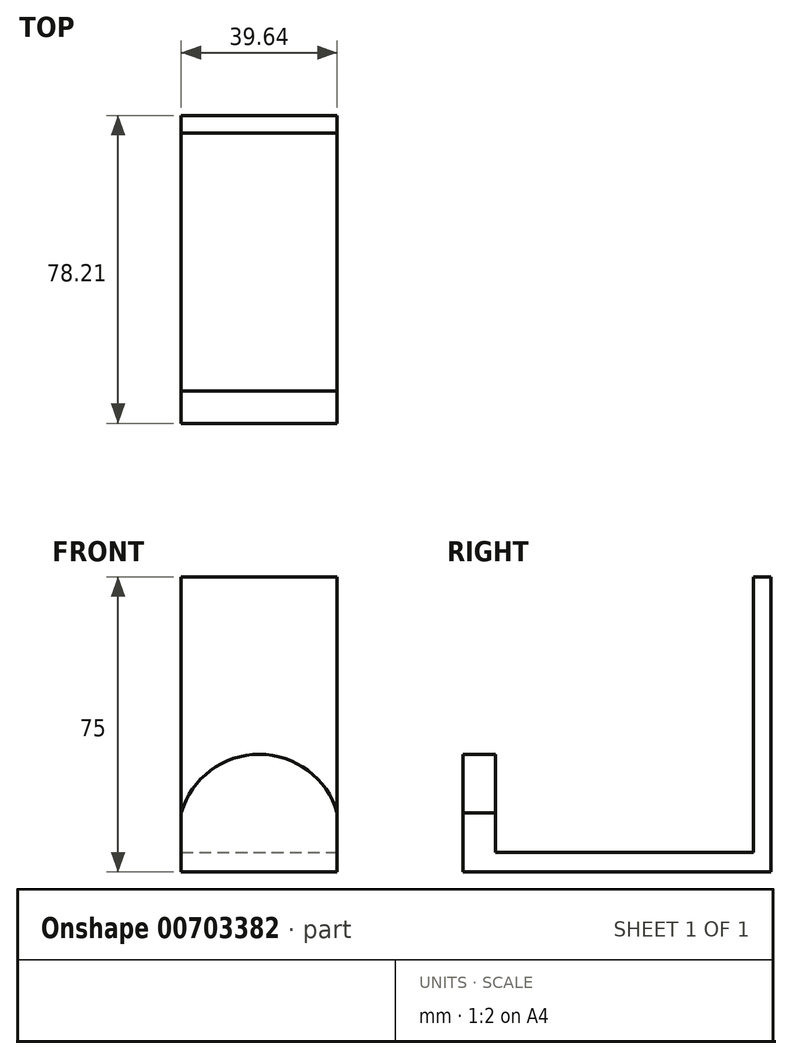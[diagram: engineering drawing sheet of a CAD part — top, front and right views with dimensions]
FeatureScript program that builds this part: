
annotation { "Feature Type Name" : "Feature", "Feature Type Description" : "" }
export const myFeature = defineFeature(function(context is Context, id is Id, definition is map)
    precondition{}
    {
        {
            var Q0;
            Q0=qCreatedBy(makeId("Top.planeOp"),FACE);
            var sketch = newSketch(context, id + "F0", { "sketchPlane" : qUnion([Q0])});
            skLineSegment(sketch, "E0.bottom", {"start": v(0, 0) * mm, "end": v(39.64, 0) * mm});
            skLineSegment(sketch, "E0.top", {"start": v(0, 78.21) * mm, "end": v(39.64, 78.21) * mm});
            skLineSegment(sketch, "E0.left", {"start": v(0, 0) * mm, "end": v(0, 78.21) * mm});
            skLineSegment(sketch, "E0.right", {"start": v(39.64, 0) * mm, "end": v(39.64, 78.21) * mm});
            skSolve(sketch);
        }
        {
            var Q0;
            Q0=makeQuery(id+"F0.imprint","IMPRINT",FACE,{"disambiguationData":[TD([[makeQuery(id+"F0.imprint","IMPRINT",EDGE,{"derivedFrom":sQuery(id+"F0.wireOp",EDGE,"E0.bottom")}),1.0]])]});
            extrude(context, id + "F1", {"entities" : qUnion([Q0]), "depth" : 5 * mm, "offsetDistance" : 25 * mm});
        }
        {
            var Q0;
            Q0=makeQuery(id+"F1.opExtrude","CAP_FACE",FACE,{"disambiguationData":[OSD([sQuery(id+"F0.wireOp",EDGE,"E0.bottom"),sQuery(id+"F0.wireOp",EDGE,"E0.top"),sQuery(id+"F0.wireOp",EDGE,"E0.left"),sQuery(id+"F0.wireOp",EDGE,"E0.right")])],"isStart":false});
            var sketch = newSketch(context, id + "F2", { "sketchPlane" : qUnion([Q0])});
            skLineSegment(sketch, "E1.bottom", {"start": v(0, 78.21) * mm, "end": v(39.64, 78.21) * mm});
            skLineSegment(sketch, "E1.top", {"start": v(0, 73.76) * mm, "end": v(39.64, 73.76) * mm});
            skLineSegment(sketch, "E1.left", {"start": v(0, 78.21) * mm, "end": v(0, 73.76) * mm});
            skLineSegment(sketch, "E1.right", {"start": v(39.64, 78.21) * mm, "end": v(39.64, 73.76) * mm});
            skSolve(sketch);
        }
        {
            var Q0;
            Q0=makeQuery(id+"F2.imprint","IMPRINT",FACE,{"disambiguationData":[TD([[makeQuery(id+"F2.imprint","IMPRINT",EDGE,{"derivedFrom":sQuery(id+"F2.wireOp",EDGE,"E1.bottom")}),-1.0]])]});
            extrude(context, id + "F3", {"entities" : qUnion([Q0]), "operationType" : NewBodyOperationType.ADD, "depth" : 70 * mm, "offsetDistance" : 25 * mm});
        }
        {
            var Q0;
            Q0=makeQuery(id+"F1.opExtrude","CAP_FACE",FACE,{"disambiguationData":[OSD([sQuery(id+"F0.wireOp",EDGE,"E0.bottom"),sQuery(id+"F0.wireOp",EDGE,"E0.top"),sQuery(id+"F0.wireOp",EDGE,"E0.left"),sQuery(id+"F0.wireOp",EDGE,"E0.right")])],"isStart":false});
            var sketch = newSketch(context, id + "F4", { "sketchPlane" : qUnion([Q0])});
            skLineSegment(sketch, "E2.bottom", {"start": v(0, 8.18) * mm, "end": v(39.64, 8.18) * mm});
            skLineSegment(sketch, "E2.top", {"start": v(0, 0) * mm, "end": v(39.64, 0) * mm});
            skLineSegment(sketch, "E2.left", {"start": v(0, 8.18) * mm, "end": v(0, 0) * mm});
            skLineSegment(sketch, "E2.right", {"start": v(39.64, 8.18) * mm, "end": v(39.64, 0) * mm});
            skSolve(sketch);
        }
        {
            var Q0;
            Q0=makeQuery(id+"F4.imprint","IMPRINT",FACE,{"disambiguationData":[TD([[makeQuery(id+"F4.imprint","IMPRINT",EDGE,{"derivedFrom":sQuery(id+"F4.wireOp",EDGE,"E2.bottom")}),-1.0]])]});
            extrude(context, id + "F5", {"entities" : qUnion([Q0]), "operationType" : NewBodyOperationType.ADD, "depth" : 25 * mm, "offsetDistance" : 25 * mm});
        }
        {
            var Q0;
            Q0=makeQuery(id+"F5.boolean.opBoolean","MERGE",FACE,{"derivedFrom":[makeQuery(id+"F1.opExtrude","SWEPT_FACE",FACE,{"disambiguationData":[OSD([sQuery(id+"F0.wireOp",EDGE,"E0.bottom")])]}),makeQuery(id+"F5.opExtrude","SWEPT_FACE",FACE,{"disambiguationData":[OSD([sQuery(id+"F4.wireOp",EDGE,"E2.top")])]})]});
            var sketch = newSketch(context, id + "F6", { "sketchPlane" : qUnion([Q0])});
            skArc(sketch, "E3", {"start": v(39.64, 15) * mm, "mid": v(19.82, 29.9) * mm, "end": v(0, 15) * mm});
            skSolve(sketch);
        }
        {
            var Q0;
            {var subQ0=sQuery(id+"F6.wireOp",EDGE,"E3");Q0=makeQuery(id+"F6.imprint","IMPRINT",FACE,{"disambiguationData":[TD([[makeQuery(id+"F6.imprint","IMPRINT",EDGE,{"derivedFrom":subQ0}),-1.0]])]});}
            extrude(context, id + "F7", {"entities" : qUnion([Q0]), "operationType" : NewBodyOperationType.REMOVE, "oppositeDirection" : true, "depth" : 25 * mm, "offsetDistance" : 25 * mm});
        }
    });
